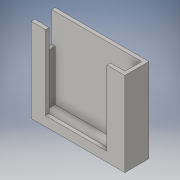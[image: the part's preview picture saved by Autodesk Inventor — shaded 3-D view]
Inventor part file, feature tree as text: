
AUTODESK INVENTOR PART (.ipt)
format: ipt  version: 2016 (Build 200138000, 138)  size: 130,560 bytes
history: native  units: mm
features: extrude x4, sketch x4
ambient origin geometry x8: Origin, YZ Plane, XZ Plane, XY Plane, X Axis, Y Axis, Z Axis, Center Point
bodies: Solid1 (feature_tree)
feature tree (8):
  extrude  "Extrusion1"  Depth=72.0mm
  extrude  "Extrusion2"  Depth=78.0mm
  extrude  "Extrusion3"  Depth=78.0mm
  extrude  "Extrusion4"  Depth=3.0mm TaperAngle=0.0deg
  sketch  "Sketch1"  dims[d0=14.0mm d1=72.0mm]
  sketch  "Sketch2"  dims[d2=20.0mm d3=78.0mm]
  sketch  "Sketch3"  dims[d4=42.0mm d5=0.0mm d6=78.0mm]
  sketch  "Sketch4"  dims[d7=51.0mm d9=10.0mm d10=0.0mm d11=25.0mm d12=0.0mm d13=3.0mm d14=0.0mm]
